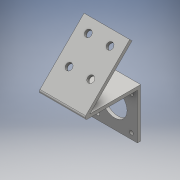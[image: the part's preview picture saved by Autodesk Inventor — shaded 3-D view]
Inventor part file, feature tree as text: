
AUTODESK INVENTOR PART (.ipt)
format: ipt  version: 2016 (Build 200138000, 138)  size: 167,424 bytes
history: native  units: mm
features: extrude x6, sketch x6, plane x1, fillet x1
ambient origin geometry x8: Origin, YZ Plane, XZ Plane, XY Plane, X Axis, Y Axis, Z Axis, Center Point
bodies: Body1 (feature_tree)
feature tree (14):
  extrude  "拉伸2"  Depth=42.0mm
  extrude  "拉伸3"  Depth=3.0mm
  plane  "工作平面1"
  extrude  "拉伸4"  TaperAngle=45.0deg  [1 undecoded]
  extrude  "拉伸5"  Depth=3.0mm TaperAngle=0.0deg
  fillet  "圆角1"  Radius=3.0mm
  extrude  "拉伸6"  Depth=2.0mm
  extrude  "拉伸7"  Depth=3.0mm
  sketch  "草图2"  dims[d3=42.0mm d4=42.0mm]
  sketch  "草图3"  dims[d5=3.0mm d6=0.0mm d7=51.0mm]
  sketch  "草图4"  dims[d8=3.0mm d9=0.0mm d10=45.0deg]
  sketch  "草图6"  dims[d11=60.0mm d12=3.0mm d13=0.0mm d14=3.0mm d15=0.0mm]
  sketch  "草图7"  dims[d16=2.0mm d17=23.0mm]
  sketch  "草图8"  dims[d18=3.5mm d19=15.5mm d20=15.5mm d21=15.5mm d22=15.5mm d23=3.0mm d24=0.0mm d25=6.0mm d26=6.0mm d27=10.0mm d28=25.0mm d29=10.0mm d30=3.0mm d31=0.0mm]
note: 1 required parameter value undecoded (feature->parameter linkage not recoverable at this tier; creation-order binding heuristic only, values carry confidence <= 0.55)
